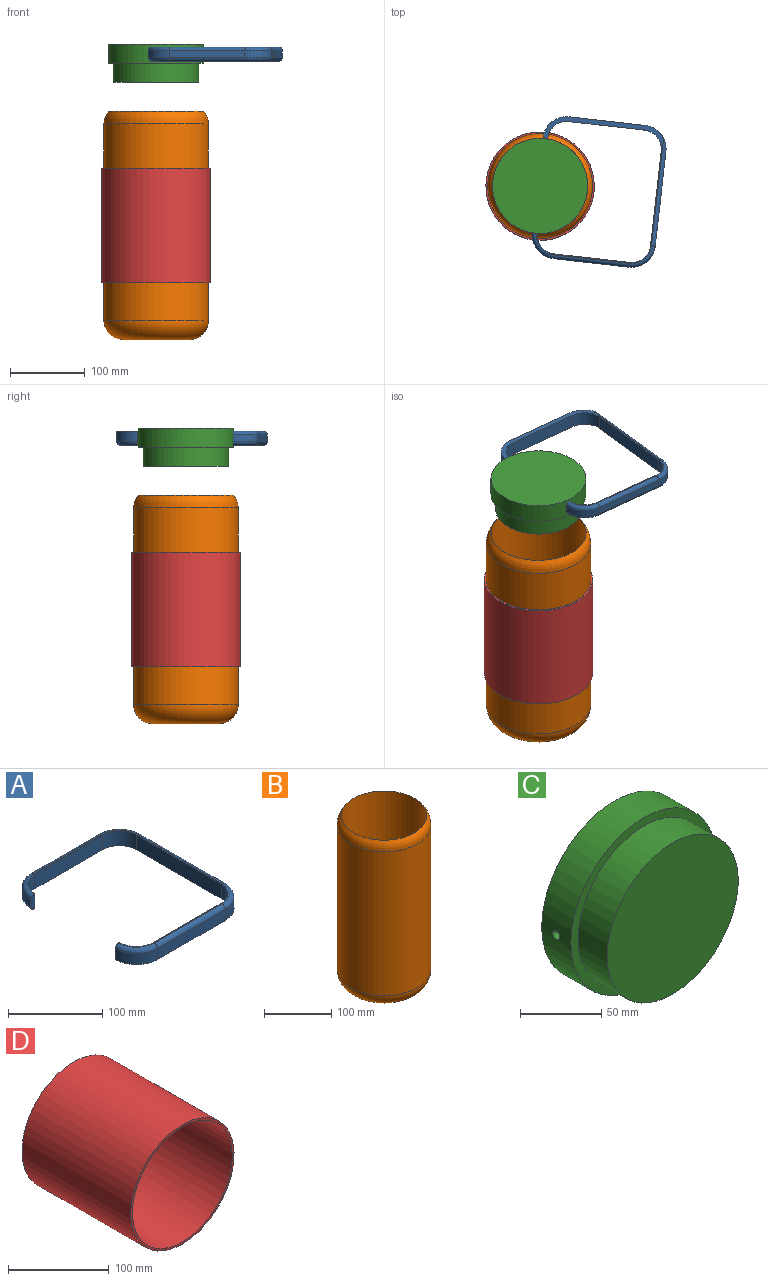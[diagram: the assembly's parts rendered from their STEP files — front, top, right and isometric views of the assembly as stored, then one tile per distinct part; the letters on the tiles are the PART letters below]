
ASSEMBLY  parts=4 mates=3
PART A: 31 faces, bbox 170.3x195.7x19.1 mm
  f0: cylinder r=25.4mm len=25.4mm, axis (0,0,-1), area 760.1mm2, adj f1,f16,f17,f18
  f1: plane 127x19.05mm, normal (-1,0,0), area 2419.3mm2, adj f0,f2,f17,f18
  f2: cylinder r=25.4mm len=25.4mm, axis (0,0,-1), area 760.1mm2, adj f1,f3,f17,f18
  f3: plane 101.6x19.05mm, normal (0,1,0), area 1935.5mm2, adj f2,f4,f17,f18
  f4: cylinder r=25.4mm len=25.4mm, axis (0,0,-1), area 760.1mm2, adj f3,f5,f17,f18
  f5: plane 19.05x6.35mm, normal (0,1,0), area 115.4mm2, adj f4,f6,f17,f18,f23
  f6: cylinder r=31.75mm len=31.75mm, axis (0,0,-1), area 696.7mm2, adj f5,f7,f18,f23
  f7: plane 101.6x13.97mm, normal (0,-1,0), area 1419.4mm2, adj f6,f8,f18,f24
  f8: cylinder r=31.75mm len=31.75mm, axis (0,0,-1), area 660.9mm2, adj f7,f9,f18,f22,f25
  f9: plane 101.6x8.91mm, normal (1,0,0), area 904.4mm2, adj f8,f10,f22,f26
  f10: plane 25.4x8.89mm, normal (1,0,0), area 225.8mm2, adj f9,f11,f22,f27
  f11: cylinder r=31.75mm len=31.75mm, axis (0,0,-1), area 443.4mm2, adj f10,f12,f21,f28
  f12: plane 101.6x8.89mm, normal (0,1,0), area 903.2mm2, adj f11,f13,f20,f29
  f13: cylinder r=31.75mm len=31.75mm, axis (0,0,-1), area 443.4mm2, adj f12,f14,f19,f30
  f14: plane 19.05x6.35mm, normal (0,-1,0), area 109.9mm2, adj f13,f15,f17,f18,f19,f30
  f15: cylinder r=25.4mm len=25.4mm, axis (0,0,-1), area 760.1mm2, adj f14,f16,f17,f18
  f16: plane 101.6x19.05mm, normal (0,-1,0), area 1935.5mm2, adj f0,f15,f17,f18
  f17: plane 180.34x154.94mm, normal (0,0,1), area 627.1mm2, adj f0,f1,f2,f3,f4,f5,f14,f15
  f18: plane 185.42x160.02mm, normal (0,0,-1), area 1550.1mm2, adj f0,f1,f2,f3,f4,f5,f6,f7
  f19: torus R=26.67mm, axis (0,0,1), area 374.8mm2, adj f13,f14,f18,f20
  f20: cylinder r=5.08mm len=101.6mm, axis (-1,0,0), area 810.7mm2, adj f12,f18,f19,f21
  f21: torus R=26.67mm, axis (0,0,1), area 374.8mm2, adj f11,f18,f20,f22
  f22: cylinder r=5.08mm len=144.23mm, axis (0,1,0), area 1086.2mm2, adj f8,f9,f10,f18,f21
  f23: torus R=26.67mm, axis (0,0,1), area 374.8mm2, adj f5,f6,f17,f24
  f24: cylinder r=5.08mm len=101.6mm, axis (-1,0,0), area 810.7mm2, adj f7,f17,f23,f25
  f25: torus R=26.67mm, axis (0,0,1), area 374.8mm2, adj f8,f17,f24,f26
  f26: cylinder r=5.08mm len=101.6mm, axis (0,-1,0), area 810.7mm2, adj f9,f17,f25,f27
  f27: cylinder r=5.08mm len=25.4mm, axis (0,-1,0), area 202.7mm2, adj f10,f17,f26,f28
  f28: torus R=26.67mm, axis (0,0,1), area 374.8mm2, adj f11,f17,f27,f29
  f29: cylinder r=5.08mm len=101.6mm, axis (1,0,0), area 810.7mm2, adj f12,f17,f28,f30
  f30: torus R=26.67mm, axis (0,0,1), area 374.8mm2, adj f13,f14,f17,f29
PART B: 7 faces, bbox 151.2x151.2x306 mm
  f0: cylinder r=63.5mm len=254mm, axis (0,0,-1), area 101341.5mm2, adj f4,f6
  f1: cylinder r=69.85mm len=262.6mm, axis (0,0,-1), area 115249.8mm2, adj f5,f6
  f2: plane 88.9x88.9mm, normal (0,0,-1), area 6207.2mm2, adj f5
  f3: plane 76.2x76.2mm, normal (0,0,1), area 4560.4mm2, adj f4
  f4: torus R=38.1mm, axis (0,0,1), area 13604.9mm2, adj f0,f3
  f5: torus R=44.45mm, axis (0,0,1), area 15196.7mm2, adj f1,f2
  f6: torus R=44.45mm, axis (0,0,1), area 7808.2mm2, adj f0,f1
PART C: 6 faces, bbox 127x50.8x127 mm
  f0: cylinder r=63.5mm len=127mm, axis (0,1,0), area 10071.1mm2, adj f1,f2,f5
  f1: plane 127x127mm, normal (0,-1,0), area 2406.9mm2, adj f0,f3
  f2: plane 127x127mm, normal (0,1,0), area 12667.7mm2, adj f0
  f3: cylinder r=57.15mm len=114.3mm, axis (0,1,0), area 9120.7mm2, adj f1,f4
  f4: plane 114.3x114.3mm, normal (0,-1,0), area 10260.8mm2, adj f3
  f5: cylinder r=3.17mm len=127mm, axis (1,0,0), area 2532mm2, adj f0
PART D: 4 faces, bbox 144.8x152.4x144.8 mm
  f0: cylinder r=69.85mm len=152.4mm, axis (0,1,0), area 66885.4mm2, adj f2,f3
  f1: cylinder r=72.39mm len=152.4mm, axis (0,1,0), area 69317.6mm2, adj f2,f3
  f2: plane 144.78x144.78mm, normal (0,-1,0), area 1135mm2, adj f0,f1
  f3: plane 144.78x144.78mm, normal (0,1,0), area 1135mm2, adj f0,f1
PLACE A rot(axis=(-1,0.06,0),180deg) t=(12.59,14.97,310.09)mm
PLACE B t=(-7.88,-24.11,-80.49)mm fixed
PLACE C rot(axis=(0.53,-0.6,-0.6),123.8deg) t=(-5.95,-6.98,313.67)mm
PLACE D rot(axis=(-1,0,0),90deg) t=(-7.88,-24.11,-4.29)mm
MATE cylindrical B.f0 <-> C.f0  axis (0,0,-1) through (-7.88,-24.11,224.31)mm
MATE fastened D.f0 <-> B.f0  axis (0,0,-1) through (-7.88,-24.11,148.11)mm
MATE revolute A.f5 <-> C.f5  axis (-0.11,-0.99,0) through (-0.68,39.75,300.97)mm
